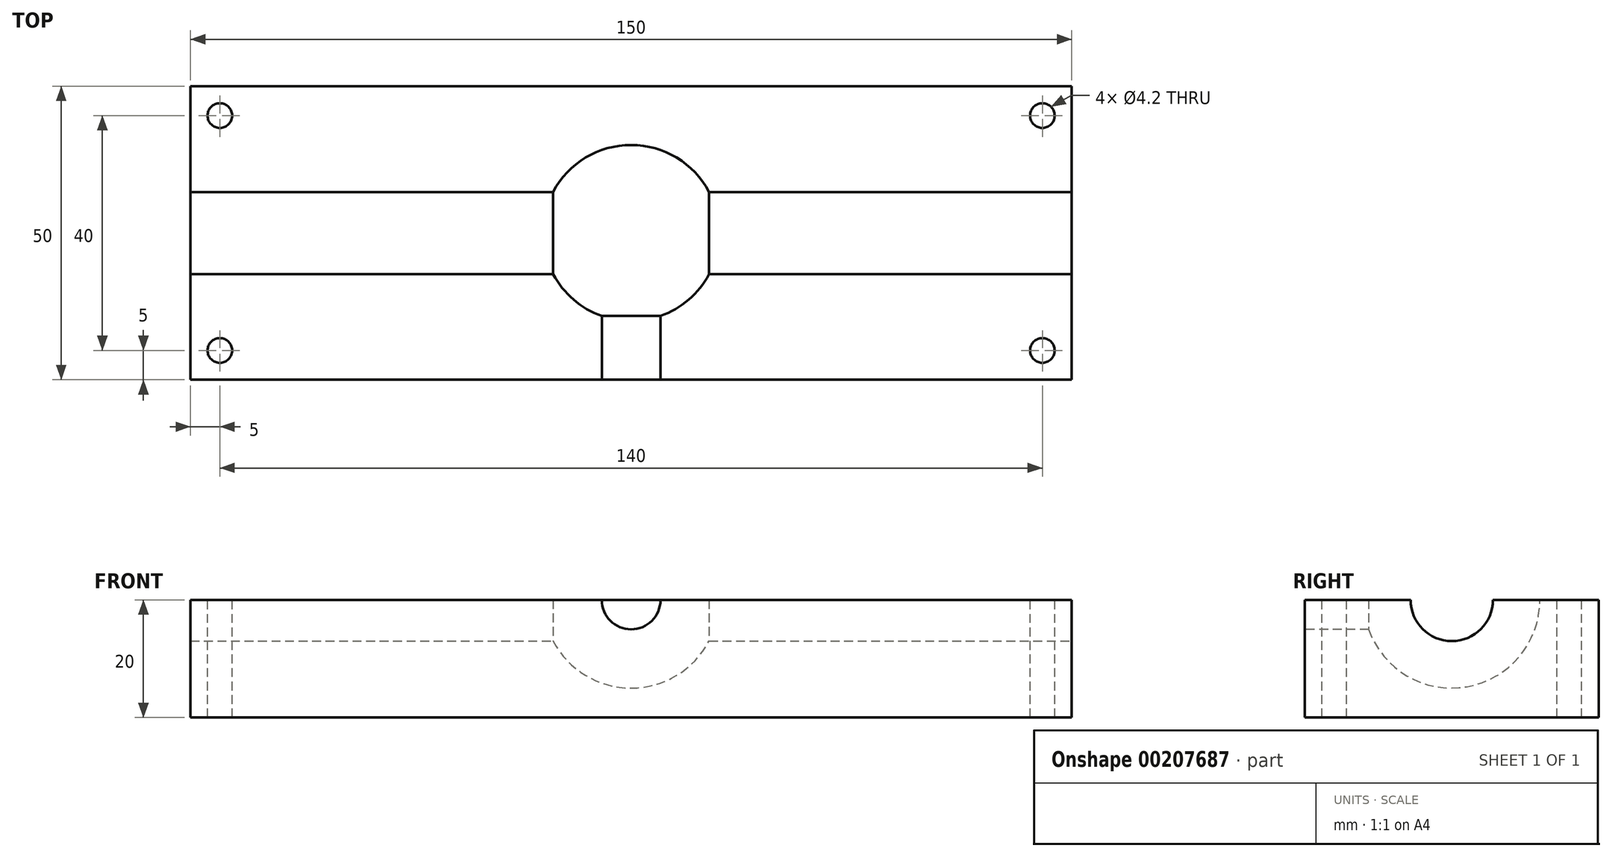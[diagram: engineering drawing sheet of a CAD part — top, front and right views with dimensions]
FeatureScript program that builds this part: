
annotation { "Feature Type Name" : "Feature", "Feature Type Description" : "" }
export const myFeature = defineFeature(function(context is Context, id is Id, definition is map)
    precondition{}
    {
        {
            var Q0;
            Q0=qCreatedBy(makeId("Front.planeOp"),FACE);
            var sketch = newSketch(context, id + "F0", { "sketchPlane" : qUnion([Q0])});
            skCircle(sketch, "E0", {"center": v(0, 0) * mm, "radius": 315 * mm, "construction": true});
            skLineSegment(sketch, "E1", {"start": v(-75, 305.94) * mm, "end": v(0, 0) * mm, "construction": true});
            skLineSegment(sketch, "E2", {"start": v(0, 0) * mm, "end": v(75, 305.94) * mm, "construction": true});
            skArc(sketch, "E3", {"start": v(75, 305.94) * mm, "mid": v(0, 315) * mm, "end": v(-75, 305.94) * mm});
            skLineSegment(sketch, "E4", {"start": v(-75, 335) * mm, "end": v(-75, 305.94) * mm});
            skLineSegment(sketch, "E5", {"start": v(75, 335) * mm, "end": v(75, 305.94) * mm});
            skLineSegment(sketch, "E6", {"start": v(-75, 335) * mm, "end": v(75, 335) * mm});
            skLineSegment(sketch, "E7", {"start": v(0, 335) * mm, "end": v(0, 0) * mm});
            skSolve(sketch);
        }
        {
            var Q0;
            Q0=makeQuery(id+"F0.imprint","IMPRINT",FACE,{"disambiguationData":[TD([[makeQuery(id+"F0.imprint","IMPRINT",EDGE,{"derivedFrom":sQuery(id+"F0.wireOp",EDGE,"E3")}),-1.0]])]});
            extrude(context, id + "F1", {"entities" : qUnion([Q0]), "endBound" : BoundingType.SYMMETRIC, "depth" : 50 * mm});
        }
        {
            var Q0;
            Q0=makeQuery(id+"F1.opExtrude","SWEPT_FACE",FACE,{"disambiguationData":[OSD([sQuery(id+"F0.wireOp",EDGE,"E6")])]});
            var sketch = newSketch(context, id + "F2", { "sketchPlane" : qUnion([Q0])});
            skLineSegment(sketch, "E8", {"start": v(-75, 0) * mm, "end": v(75, 0) * mm, "construction": true});
            skLineSegment(sketch, "E9.bottom", {"start": v(-75, 7) * mm, "end": v(-13.27, 7) * mm});
            skLineSegment(sketch, "E9.top", {"start": v(-75, 0) * mm, "end": v(-13.27, 0) * mm});
            skLineSegment(sketch, "E9.left", {"start": v(-75, 7) * mm, "end": v(-75, 0) * mm});
            skLineSegment(sketch, "E9.right", {"start": v(-13.27, 7) * mm, "end": v(-13.27, 0) * mm, "construction": true});
            skArc(sketch, "E10", {"start": v(15, 0) * mm, "mid": v(0, 15) * mm, "end": v(-15, 0) * mm});
            skLineSegment(sketch, "E11.bottom", {"start": v(13.27, 7) * mm, "end": v(75, 7) * mm});
            skLineSegment(sketch, "E11.top", {"start": v(13.27, 0) * mm, "end": v(75, 0) * mm});
            skLineSegment(sketch, "E11.left", {"start": v(13.27, 7) * mm, "end": v(13.27, 0) * mm, "construction": true});
            skLineSegment(sketch, "E11.right", {"start": v(75, 7) * mm, "end": v(75, 0) * mm});
            skLineSegment(sketch, "E12", {"start": v(-15, 0) * mm, "end": v(15, 0) * mm});
            skSolve(sketch);
        }
        {
            var Q0;
            {var subQ0=sQuery(id+"F2.wireOp",EDGE,"E9.bottom");Q0=makeQuery(id+"F2.imprint","IMPRINT",FACE,{"disambiguationData":[TD([[makeQuery(id+"F2.imprint","IMPRINT",EDGE,{"derivedFrom":subQ0}),-1.0]])]});}
            var Q1;
            {var subQ2=sQuery(id+"F2.wireOp",EDGE,"E12");var subQ4=makeQuery(id+"F2.imprint","IMPRINT",VERTEX,{"disambiguationData":[OD(0.0)],"derivedFrom":subQ2});Q1=makeQuery(id+"F2.imprint","IMPRINT",FACE,{"disambiguationData":[TD([[makeQuery(id+"F2.imprint","IMPRINT",EDGE,{"disambiguationData":[TD([[subQ4,-1.0]])],"derivedFrom":subQ2}),1.0]])]});}
            var Q2;
            {var subQ2=sQuery(id+"F2.wireOp",EDGE,"E11.bottom");Q2=makeQuery(id+"F2.imprint","IMPRINT",FACE,{"disambiguationData":[TD([[makeQuery(id+"F2.imprint","IMPRINT",EDGE,{"derivedFrom":subQ2}),-1.0]])]});}
            var Q3;
            Q3=sQuery(id+"F2.wireOp",EDGE,"E9.top");
            revolve(context, id + "F3", {"operationType" : NewBodyOperationType.REMOVE, "entities" : qUnion([Q0, Q1, Q2]), "axis" : qUnion([Q3]), "revolveType" : RevolveType.FULL, "oppositeDirection" : true});
        }
        {
            var Q0;
            {var subQ0=sQuery(id+"F0.wireOp",EDGE,"E5");var subQ1=sQuery(id+"F0.wireOp",EDGE,"E6");var subQ2=sQuery(id+"F0.wireOp",EDGE,"E4");Q0=makeQuery(id+"F3.boolean.opBoolean","SPLIT",FACE,{"disambiguationData":[TD([makeQuery(id+"F1.opExtrude","CAP_FACE",FACE,{"disambiguationData":[OSD([sQuery(id+"F0.wireOp",EDGE,"E3"),subQ2,subQ0,subQ1])],"isStart":true})])],"derivedFrom":makeQuery(id+"F1.opExtrude","SWEPT_FACE",FACE,{"disambiguationData":[OSD([subQ1])]})});}
            var sketch = newSketch(context, id + "F4", { "sketchPlane" : qUnion([Q0])});
            skCircle(sketch, "E13", {"center": v(-70, 20) * mm, "radius": 5 * mm});
            skCircle(sketch, "E14", {"center": v(-70, -20) * mm, "radius": 5 * mm});
            skCircle(sketch, "E15", {"center": v(70, -20) * mm, "radius": 5 * mm});
            skCircle(sketch, "E16", {"center": v(70, 20) * mm, "radius": 5 * mm});
            skSolve(sketch);
        }
        {
            var Q0;
            Q0=sQuery(id+"F4.wireOp",VERTEX,"E13.center");
            var Q1;
            Q1=sQuery(id+"F4.wireOp",VERTEX,"E14.center");
            var Q2;
            Q2=sQuery(id+"F4.wireOp",VERTEX,"E16.center");
            var Q3;
            Q3=sQuery(id+"F4.wireOp",VERTEX,"E15.center");
            var Q4;
            Q4=makeQuery(id+"F1.opExtrude","SWEPT_BODY",BODY,{"disambiguationData":[OSD([sQuery(id+"F0.wireOp",EDGE,"E3"),sQuery(id+"F0.wireOp",EDGE,"E4"),sQuery(id+"F0.wireOp",EDGE,"E5"),sQuery(id+"F0.wireOp",EDGE,"E6")])]});
            hole(context, id + "F5", {"style" : HoleStyle.SIMPLE, "endStyle" : HoleEndStyle.BLIND, "standardTappedOrClearance" : lookupTablePath({ "standard" : "ISO", "engagement" : "75%", "pitch" : "0.8 mm", "size" : "M5", "type" : "Tapped" }), "standardBlindInLast" : lookupTablePath({ "standard" : "ISO", "engagement" : "75%", "pitch" : "0.8 mm", "size" : "M5", "type" : "Tapped" }), "holeDiameter" : 4.2 * mm, "showTappedDepth" : true, "holeDepth" : 20 * mm, "tappedDepth" : 17.6 * mm, "tapClearance" : 3, "locations" : qUnion([Q0, Q1, Q2, Q3]), "scope" : qUnion([Q4]), "majorDiameter" : 5 * mm});
        }
        {
            var Q0;
            {var subQ0=sQuery(id+"F0.wireOp",EDGE,"E5");var subQ1=sQuery(id+"F0.wireOp",EDGE,"E4");var subQ2=sQuery(id+"F0.wireOp",EDGE,"E6");Q0=makeQuery(id+"F3.boolean.opBoolean","SPLIT",FACE,{"disambiguationData":[TD([makeQuery(id+"F1.opExtrude","CAP_FACE",FACE,{"disambiguationData":[OSD([sQuery(id+"F0.wireOp",EDGE,"E3"),subQ1,subQ0,subQ2])],"isStart":false})])],"derivedFrom":makeQuery(id+"F1.opExtrude","SWEPT_FACE",FACE,{"disambiguationData":[OSD([subQ2])]})});}
            var sketch = newSketch(context, id + "F6", { "sketchPlane" : qUnion([Q0])});
            skLineSegment(sketch, "E17.bottom", {"start": v(-5, 0) * mm, "end": v(0, 0) * mm});
            skLineSegment(sketch, "E17.top", {"start": v(-5, -25) * mm, "end": v(0, -25) * mm});
            skLineSegment(sketch, "E17.left", {"start": v(-5, 0) * mm, "end": v(-5, -25) * mm});
            skLineSegment(sketch, "E17.right", {"start": v(0, 0) * mm, "end": v(0, -25) * mm});
            skSolve(sketch);
        }
        {
            var Q0;
            {var subQ0=sQuery(id+"F6.wireOp",EDGE,"E17.bottom");Q0=makeQuery(id+"F6.imprint","IMPRINT",FACE,{"disambiguationData":[TD([[makeQuery(id+"F6.imprint","IMPRINT",EDGE,{"derivedFrom":subQ0}),-1.0]])]});}
            var Q1;
            {var subQ0=sQuery(id+"F6.wireOp",EDGE,"E17.top");Q1=makeQuery(id+"F6.imprint","IMPRINT",FACE,{"disambiguationData":[TD([[makeQuery(id+"F6.imprint","IMPRINT",EDGE,{"derivedFrom":subQ0}),1.0]])]});}
            var Q2;
            Q2=sQuery(id+"F6.wireOp",EDGE,"E17.right");
            revolve(context, id + "F7", {"operationType" : NewBodyOperationType.REMOVE, "entities" : qUnion([Q0, Q1]), "axis" : qUnion([Q2]), "revolveType" : RevolveType.FULL, "oppositeDirection" : true});
        }
        {
            var Q0;
            Q0=makeQuery(id+"F1.opExtrude","CAP_FACE",FACE,{"disambiguationData":[OSD([sQuery(id+"F0.wireOp",EDGE,"E3"),sQuery(id+"F0.wireOp",EDGE,"E4"),sQuery(id+"F0.wireOp",EDGE,"E5"),sQuery(id+"F0.wireOp",EDGE,"E6")])],"isStart":false});
            var sketch = newSketch(context, id + "F8", { "sketchPlane" : qUnion([Q0])});
            skSolve(sketch);
        }
        {
            var Q0;
            {var subQ4=sQuery(id+"F0.wireOp",EDGE,"E3");Q0=makeQuery(id+"F8.imprint","IMPRINT",FACE,{"disambiguationData":[TD([[makeQuery(id+"F8.imprint","IMPRINT",EDGE,{"derivedFrom":makeQuery(id+"F1.opExtrude","CAP_EDGE",EDGE,{"disambiguationData":[OSD([subQ4])],"isStart":false})}),-1.0]])]});}
            var sketch = newSketch(context, id + "F9", { "sketchPlane" : qUnion([Q0])});
            skLineSegment(sketch, "E18.bottom", {"start": v(75, 305.94) * mm, "end": v(-75, 305.94) * mm});
            skLineSegment(sketch, "E18.top", {"start": v(75, 315) * mm, "end": v(-75, 315) * mm});
            skLineSegment(sketch, "E18.left", {"start": v(75, 305.94) * mm, "end": v(75, 315) * mm});
            skLineSegment(sketch, "E18.right", {"start": v(-75, 305.94) * mm, "end": v(-75, 315) * mm});
            skSolve(sketch);
        }
        {
            var Q0;
            {var subQ0=sQuery(id+"F9.wireOp",EDGE,"E18.left");Q0=makeQuery(id+"F9.imprint","IMPRINT",FACE,{"disambiguationData":[TD([[makeQuery(id+"F9.imprint","IMPRINT",EDGE,{"derivedFrom":subQ0}),-1.0]])]});}
            var Q1;
            {var subQ0=sQuery(id+"F9.wireOp",EDGE,"E18.right");Q1=makeQuery(id+"F9.imprint","IMPRINT",FACE,{"disambiguationData":[TD([[makeQuery(id+"F9.imprint","IMPRINT",EDGE,{"derivedFrom":subQ0}),1.0]])]});}
            extrude(context, id + "F10", {"entities" : qUnion([Q0, Q1]), "operationType" : NewBodyOperationType.REMOVE, "endBound" : BoundingType.THROUGH_ALL, "oppositeDirection" : true, "depth" : 25 * mm});
        }
    });
